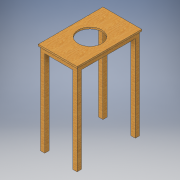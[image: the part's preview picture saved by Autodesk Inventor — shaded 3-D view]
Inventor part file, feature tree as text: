
AUTODESK INVENTOR PART (.ipt)
format: ipt  version: 2018 (Build 220112000, 112)  size: 183,296 bytes
history: native  units: in
note: dims shown in document units (in); Inventor stores cm internally (conversion verified against a paired STEP export)
features: extrude x4, sketch x4
ambient origin geometry x8: Origin, YZ Plane, XZ Plane, XY Plane, X Axis, Y Axis, Z Axis, Center Point
bodies: Solid1 (feature_tree)
feature tree (8):
  extrude  "Extrusion1"  Depth=60.0in
  extrude  "Extrusion2"  Depth=30.0in
  extrude  "Extrusion3"  Depth=4.0in
  extrude  "Extrusion4"  Depth=4.0in
  sketch  "Sketch1"  dims[d0=36.0in d1=60.0in]
  sketch  "Sketch2"  dims[d2=1.5in d3=0.0in d6=30.0in]
  sketch  "Sketch3"  dims[d7=54.0in d8=4.0in]
  sketch  "Sketch4"  dims[d9=4.0in d10=4.0in d11=4.0in d12=4.0in d13=4.0in d14=4.0in d15=4.0in d16=84.0in d17=0.0in d18=2.0in d19=50.0in d20=2.0in d21=4.0in d22=0.0in d23=22.0in d24=4.0in d25=0.0in]
